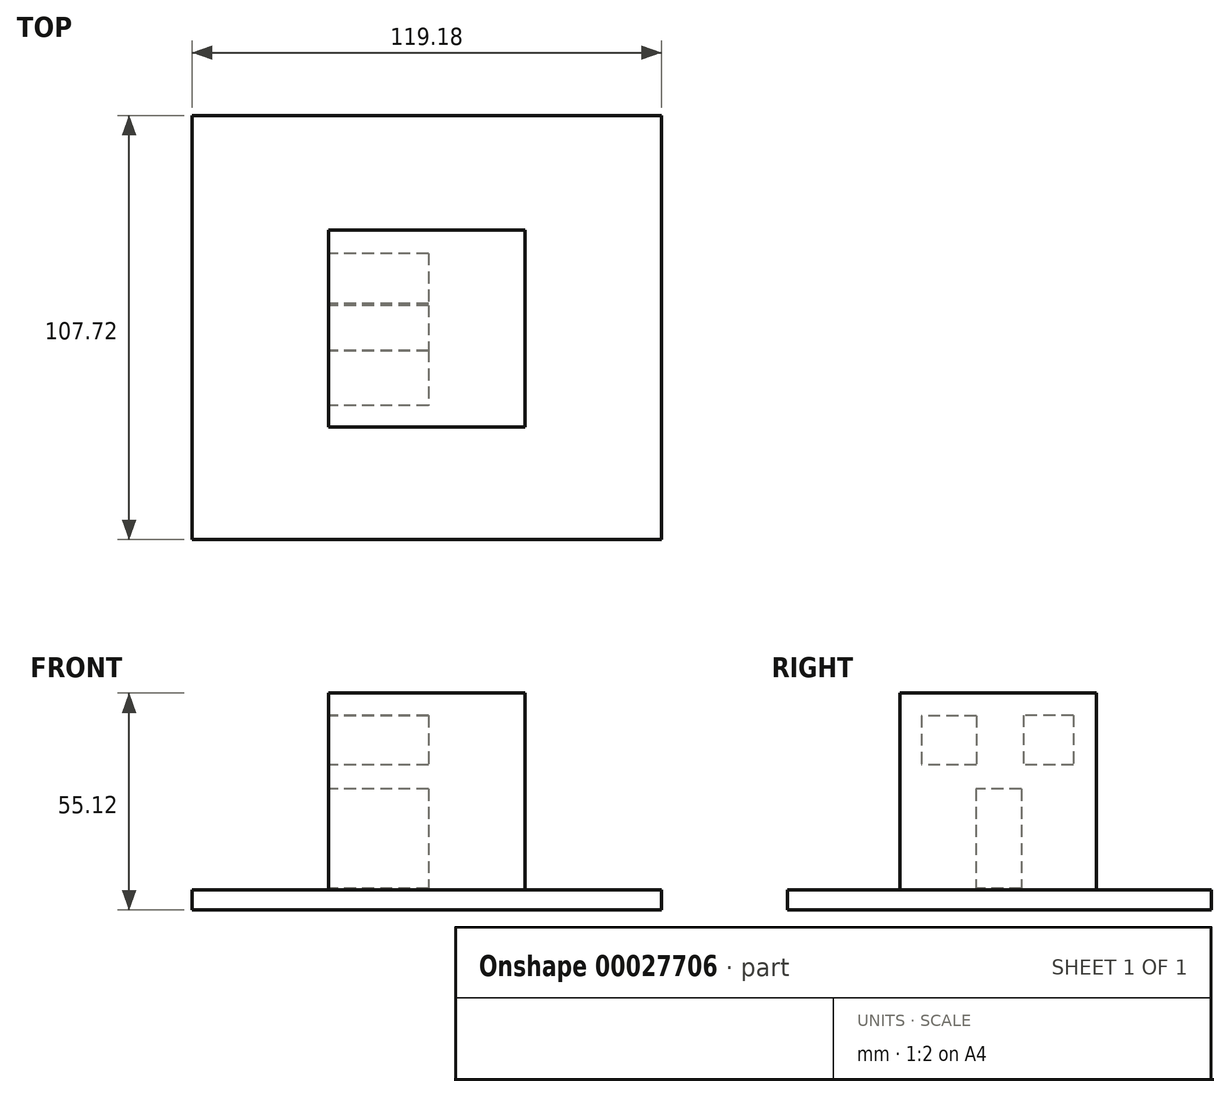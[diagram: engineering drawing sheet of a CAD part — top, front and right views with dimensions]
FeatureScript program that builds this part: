
annotation { "Feature Type Name" : "Feature", "Feature Type Description" : "" }
export const myFeature = defineFeature(function(context is Context, id is Id, definition is map)
    precondition{}
    {
        {
            var Q0;
            Q0=qCreatedBy(makeId("Top.planeOp"),FACE);
            var sketch = newSketch(context, id + "F0", { "sketchPlane" : qUnion([Q0])});
            skLineSegment(sketch, "E0.bottom", {"start": v(-24.99, 24.73) * mm, "end": v(25.01, 24.73) * mm});
            skLineSegment(sketch, "E0.top", {"start": v(-24.99, -25.27) * mm, "end": v(25.01, -25.27) * mm});
            skLineSegment(sketch, "E0.left", {"start": v(-24.99, 24.73) * mm, "end": v(-24.99, -25.27) * mm});
            skLineSegment(sketch, "E0.right", {"start": v(25.01, 24.73) * mm, "end": v(25.01, -25.27) * mm});
            skLineSegment(sketch, "E1", {"start": v(-24.99, 24.73) * mm, "end": v(25.01, -25.27) * mm, "construction": true});
            skLineSegment(sketch, "E2", {"start": v(25.01, 24.73) * mm, "end": v(-24.99, -25.27) * mm, "construction": true});
            skLineSegment(sketch, "E3", {"start": v(-24.99, 0) * mm, "end": v(25.01, 0) * mm, "construction": true});
            skLineSegment(sketch, "E4.bottom", {"start": v(-24.99, 24.73) * mm, "end": v(25.01, 24.73) * mm, "construction": true});
            skLineSegment(sketch, "E4.left", {"start": v(-24.99, 24.73) * mm, "end": v(-24.99, 0) * mm, "construction": true});
            skLineSegment(sketch, "E4.right", {"start": v(25.01, 24.73) * mm, "end": v(25.01, 0) * mm, "construction": true});
            skLineSegment(sketch, "E5", {"start": v(-24.99, 12.37) * mm, "end": v(25.01, 12.37) * mm, "construction": true});
            skLineSegment(sketch, "E6.rect.bottom", {"start": v(-18.96, 18.7) * mm, "end": v(-6.28, 18.7) * mm});
            skLineSegment(sketch, "E6.rect.top", {"start": v(-18.96, 6.03) * mm, "end": v(-6.28, 6.03) * mm});
            skLineSegment(sketch, "E6.rect.left", {"start": v(-18.96, 18.7) * mm, "end": v(-18.96, 6.03) * mm});
            skLineSegment(sketch, "E6.rect.right", {"start": v(-6.28, 18.7) * mm, "end": v(-6.28, 6.03) * mm});
            skPoint(sketch, "E6.rect.middle", {"position": v(-12.62, 12.37) * mm});
            skLineSegment(sketch, "E7.rect.bottom", {"start": v(5.68, 18.6) * mm, "end": v(19.62, 18.6) * mm});
            skLineSegment(sketch, "E7.rect.top", {"start": v(5.68, 6.14) * mm, "end": v(19.62, 6.14) * mm});
            skLineSegment(sketch, "E7.rect.left", {"start": v(5.68, 18.6) * mm, "end": v(5.68, 6.14) * mm});
            skLineSegment(sketch, "E7.rect.right", {"start": v(19.62, 18.6) * mm, "end": v(19.62, 6.14) * mm});
            skPoint(sketch, "E7.rect.middle", {"position": v(12.65, 12.37) * mm});
            skLineSegment(sketch, "E8", {"start": v(0.01, -25.27) * mm, "end": v(0, 0) * mm});
            skLineSegment(sketch, "E9.rect.bottom", {"start": v(-5.78, 0) * mm, "end": v(5.8, 0) * mm});
            skLineSegment(sketch, "E9.rect.top", {"start": v(-5.78, -25.27) * mm, "end": v(5.8, -25.27) * mm});
            skLineSegment(sketch, "E9.rect.left", {"start": v(-5.78, 0) * mm, "end": v(-5.78, -25.27) * mm});
            skLineSegment(sketch, "E9.rect.right", {"start": v(5.8, 0) * mm, "end": v(5.8, -25.27) * mm});
            skPoint(sketch, "E9.rect.middle", {"position": v(0, -12.63) * mm});
            skSolve(sketch);
        }
        {
            var Q0;
            Q0=makeQuery(id+"F0.imprint","IMPRINT",FACE,{"disambiguationData":[TD([[makeQuery(id+"F0.imprint","IMPRINT",EDGE,{"derivedFrom":sQuery(id+"F0.wireOp",EDGE,"E0.bottom")}),-1.0]])]});
            var Q1;
            Q1=makeQuery(id+"F0.imprint","IMPRINT",FACE,{"disambiguationData":[TD([[makeQuery(id+"F0.imprint","IMPRINT",EDGE,{"derivedFrom":sQuery(id+"F0.wireOp",EDGE,"E6.rect.bottom")}),-1.0]])]});
            var Q2;
            Q2=makeQuery(id+"F0.imprint","IMPRINT",FACE,{"disambiguationData":[TD([[makeQuery(id+"F0.imprint","IMPRINT",EDGE,{"derivedFrom":sQuery(id+"F0.wireOp",EDGE,"E7.rect.bottom")}),-1.0]])]});
            var Q3;
            {var subQ2=sQuery(id+"F0.wireOp",EDGE,"E8");Q3=makeQuery(id+"F0.imprint","IMPRINT",FACE,{"disambiguationData":[TD([[makeQuery(id+"F0.imprint","IMPRINT",EDGE,{"derivedFrom":subQ2}),-1.0]])]});}
            var Q4;
            {var subQ2=sQuery(id+"F0.wireOp",EDGE,"E8");Q4=makeQuery(id+"F0.imprint","IMPRINT",FACE,{"disambiguationData":[TD([[makeQuery(id+"F0.imprint","IMPRINT",EDGE,{"derivedFrom":subQ2}),1.0]])]});}
            extrude(context, id + "F1", {"entities" : qUnion([Q0, Q1, Q2, Q3, Q4]), "depth" : 50 * mm});
        }
        {
            var Q0;
            Q0=makeQuery(id+"F1.opExtrude","SWEPT_FACE",FACE,{"disambiguationData":[OSD([sQuery(id+"F0.wireOp",EDGE,"E0.left")])]});
            var sketch = newSketch(context, id + "F2", { "sketchPlane" : qUnion([Q0])});
            skLineSegment(sketch, "E10.rect.top", {"start": v(-18.82, 31.67) * mm, "end": v(-6.14, 31.67) * mm});
            skLineSegment(sketch, "E10.rect.right", {"start": v(-6.14, 44.35) * mm, "end": v(-6.14, 31.67) * mm});
            skLineSegment(sketch, "E10.rect.bottom", {"start": v(-18.82, 44.35) * mm, "end": v(-6.14, 44.35) * mm});
            skLineSegment(sketch, "E10.rect.left", {"start": v(-18.82, 44.35) * mm, "end": v(-18.82, 31.67) * mm});
            skLineSegment(sketch, "E11.rect.top", {"start": v(5.82, 31.78) * mm, "end": v(19.76, 31.78) * mm});
            skLineSegment(sketch, "E11.rect.left", {"start": v(5.82, 44.24) * mm, "end": v(5.82, 31.78) * mm});
            skLineSegment(sketch, "E11.rect.bottom", {"start": v(5.82, 44.24) * mm, "end": v(19.76, 44.24) * mm});
            skLineSegment(sketch, "E11.rect.right", {"start": v(19.76, 44.24) * mm, "end": v(19.76, 31.78) * mm});
            skLineSegment(sketch, "E12.rect.right", {"start": v(5.93, 25.64) * mm, "end": v(5.93, 0.38) * mm});
            skLineSegment(sketch, "E12.rect.bottom", {"start": v(-5.63, 25.64) * mm, "end": v(5.93, 25.64) * mm});
            skLineSegment(sketch, "E12.rect.left", {"start": v(-5.63, 25.64) * mm, "end": v(-5.63, 0.38) * mm});
            skLineSegment(sketch, "E12.rect.top", {"start": v(-5.63, 0.38) * mm, "end": v(5.93, 0.38) * mm});
            skSolve(sketch);
        }
        {
            var Q0;
            Q0=makeQuery(id+"F2.imprint","IMPRINT",FACE,{"disambiguationData":[TD([[makeQuery(id+"F2.imprint","IMPRINT",EDGE,{"derivedFrom":sQuery(id+"F2.wireOp",EDGE,"E12.rect.right")}),-1.0]])]});
            var Q1;
            Q1=makeQuery(id+"F2.imprint","IMPRINT",FACE,{"disambiguationData":[TD([[makeQuery(id+"F2.imprint","IMPRINT",EDGE,{"derivedFrom":sQuery(id+"F2.wireOp",EDGE,"E10.rect.top")}),1.0]])]});
            var Q2;
            Q2=makeQuery(id+"F2.imprint","IMPRINT",FACE,{"disambiguationData":[TD([[makeQuery(id+"F2.imprint","IMPRINT",EDGE,{"derivedFrom":sQuery(id+"F2.wireOp",EDGE,"E11.rect.top")}),1.0]])]});
            var Q3;
            Q3=sQuery(id+"F2.wireOp",EDGE,"E10.rect.top");
            var Q4;
            Q4=sQuery(id+"F2.wireOp",EDGE,"E10.rect.right");
            var Q5;
            Q5=sQuery(id+"F2.wireOp",EDGE,"E10.rect.bottom");
            var Q6;
            Q6=sQuery(id+"F2.wireOp",EDGE,"E10.rect.left");
            var Q7;
            Q7=sQuery(id+"F2.wireOp",EDGE,"E11.rect.top");
            var Q8;
            Q8=sQuery(id+"F2.wireOp",EDGE,"E11.rect.left");
            var Q9;
            Q9=sQuery(id+"F2.wireOp",EDGE,"E11.rect.bottom");
            var Q10;
            Q10=sQuery(id+"F2.wireOp",EDGE,"E11.rect.right");
            var Q11;
            Q11=sQuery(id+"F2.wireOp",EDGE,"E12.rect.right");
            var Q12;
            Q12=sQuery(id+"F2.wireOp",EDGE,"E12.rect.bottom");
            var Q13;
            Q13=sQuery(id+"F2.wireOp",EDGE,"E12.rect.left");
            var Q14;
            Q14=sQuery(id+"F2.wireOp",EDGE,"E12.rect.top");
            extrude(context, id + "F3", {"entities" : qUnion([Q0, Q1, Q2]), "operationType" : NewBodyOperationType.REMOVE, "surfaceEntities" : qUnion([Q3, Q4, Q5, Q6, Q7, Q8, Q9, Q10, Q11, Q12, Q13, Q14]), "oppositeDirection" : true, "depth" : 25.4 * mm});
        }
        {
            var Q0;
            Q0=qCreatedBy(makeId("Top.planeOp"),FACE);
            var sketch = newSketch(context, id + "F4", { "sketchPlane" : qUnion([Q0])});
            skLineSegment(sketch, "E13.rect.bottom", {"start": v(59.59, 53.86) * mm, "end": v(-59.59, 53.86) * mm});
            skLineSegment(sketch, "E13.rect.top", {"start": v(59.59, -53.86) * mm, "end": v(-59.59, -53.86) * mm});
            skLineSegment(sketch, "E13.rect.left", {"start": v(59.59, 53.86) * mm, "end": v(59.59, -53.86) * mm});
            skLineSegment(sketch, "E13.rect.right", {"start": v(-59.59, 53.86) * mm, "end": v(-59.59, -53.86) * mm});
            skPoint(sketch, "E13.rect.middle", {"position": v(0, 0) * mm});
            skSolve(sketch);
        }
        {
            var Q0;
            Q0=makeQuery(id+"F4.imprint","IMPRINT",FACE,{"disambiguationData":[TD([[makeQuery(id+"F4.imprint","IMPRINT",EDGE,{"derivedFrom":sQuery(id+"F4.wireOp",EDGE,"E13.rect.bottom")}),1.0]])]});
            extrude(context, id + "F5", {"entities" : qUnion([Q0]), "operationType" : NewBodyOperationType.ADD, "oppositeDirection" : true, "depth" : 5.12 * mm});
        }
    });
